# Revit family: HEE-D
name_source: partatom
category: Mechanical Equipment
units: mm (PartAtom-declared; Revit-internal decimal feet)

## family parameters
Always vertical = Yes
Cut with Voids When Loaded = No
Part Type = Normal
Room Calculation Point = No
Round Connector Dimension = Use Diameter
Shared = No
Work Plane-Based = No

## types (7) — shared parameters
0 = 0' - 0"
1" = 0' - 1"
1.5 = 0' - 1 1/2"
2" = 0' - 2"
2' = 2' - 0"
4" = 0' - 4"
Manufacturer = Loren Cook Company
Model = HEE-D
ONE EIGTH = 0' - 0 1/8"
Type Comments = Hooded Exhaust Ventilator Extruded Aluminum Propeller Roof Mounted/Direct Drive
URL = www.lorencook.com

## per-type parameters (varying)
| type | (A-C)/2 | (T_SQ/2)+.125" | (T_SQ/2)-2" | -(A/2) | -(C/2) | -L/2 | A | A-1.5" | A-C | A/2 | B | B-.125" | B/2 | C | C/2 | L | L/2 | RO | RO/2 | T_SQ | T_SQ/2 | W | W/2 |
| 20-HEE-D | 0' - 8 5/8" | 1' - 4 1/8" | 1' - 2" | -1' - 1 5/8" | -0' - 5" | -2' - 2" | 2' - 3 1/4" | 2' - 1 3/4" | 1' - 5 1/4" | 1' - 1 5/8" | 0' - 2" | 0' - 1 7/8" | 0' - 1" | 0' - 10" | 0' - 5" | 4' - 4" | 2' - 2" | 2' - 3 1/2" | 1' - 1 3/4" | 2' - 8" | 1' - 4" | 4' - 4" | 2' - 2" |
| 30-HEE-D | 0' - 10 1/4" | 1' - 9 1/8" | 1' - 7" | -1' - 3 1/4" | -0' - 5" | -2' - 10 1/2" | 2' - 6 1/2" | 2' - 5" | 1' - 8 1/2" | 1' - 3 1/4" | 0' - 3" | 0' - 2 7/8" | 0' - 1 1/2" | 0' - 10" | 0' - 5" | 5' - 9" | 2' - 10 1/2" | 3' - 1 1/2" | 1' - 6 3/4" | 3' - 6" | 1' - 9" | 5' - 9" | 2' - 10 1/2" |
| 36-HEE-D | 0' - 11 1/2" | 2' - 0 1/8" | 1' - 10" | -1' - 4 1/2" | -0' - 5" | -3' - 4" | 2' - 9" | 2' - 7 1/2" | 1' - 11" | 1' - 4 1/2" | 0' - 3" | 0' - 2 7/8" | 0' - 1 1/2" | 0' - 10" | 0' - 5" | 6' - 8" | 3' - 4" | 3' - 7 1/2" | 1' - 9 3/4" | 4' - 0" | 2' - 0" | 6' - 8" | 3' - 4" |
| 42-HEE-D | 1' - 2" | 2' - 3 1/8" | 2' - 1" | -1' - 7" | -0' - 5" | -3' - 9" | 3' - 2" | 3' - 0 1/2" | 2' - 4" | 1' - 7" | 0' - 3" | 0' - 2 7/8" | 0' - 1 1/2" | 0' - 10" | 0' - 5" | 7' - 6" | 3' - 9" | 4' - 1 1/2" | 2' - 0 3/4" | 4' - 6" | 2' - 3" | 7' - 6" | 3' - 9" |
| 48-HEE-D | 1' - 2" | 2' - 6 1/8" | 2' - 4" | -1' - 8 3/4" | -0' - 6 3/4" | -4' - 7" | 3' - 5 1/2" | 3' - 4" | 2' - 4" | 1' - 8 3/4" | 0' - 3" | 0' - 2 7/8" | 0' - 1 1/2" | 1' - 1 1/2" | 0' - 6 3/4" | 9' - 2" | 4' - 7" | 4' - 7 1/2" | 2' - 3 3/4" | 5' - 0" | 2' - 6" | 7' - 6" | 3' - 9" |
| 54-HEE-D | 1' - 2 7/8" | 2' - 9 1/8" | 2' - 7" | -1' - 10 1/4" | -0' - 7 3/8" | -4' - 7 1/2" | 3' - 8 1/2" | 3' - 7" | 2' - 5 3/4" | 1' - 10 1/4" | 0' - 3" | 0' - 2 7/8" | 0' - 1 1/2" | 1' - 2 3/4" | 0' - 7 3/8" | 9' - 3" | 4' - 7 1/2" | 5' - 1 1/2" | 2' - 6 3/4" | 5' - 6" | 2' - 9" | 9' - 1" | 4' - 6 1/2" |
| 24-HEE-D | 0' - 9 3/8" | 1' - 6 1/8" | 1' - 4" | -1' - 2 3/8" | -0' - 5" | -2' - 5 1/2" | 2' - 4 3/4" | 2' - 3 1/4" | 1' - 6 3/4" | 1' - 2 3/8" | 0' - 3" | 0' - 2 7/8" | 0' - 1 1/2" | 0' - 10" | 0' - 5" | 4' - 11" | 2' - 5 1/2" | 2' - 7 1/2" | 1' - 3 3/4" | 3' - 0" | 1' - 6" | 4' - 11" | 2' - 5 1/2" |

## geometry (parser evidence)
native form markers: Sweep x2
no freeform markers — native parametric forms only
